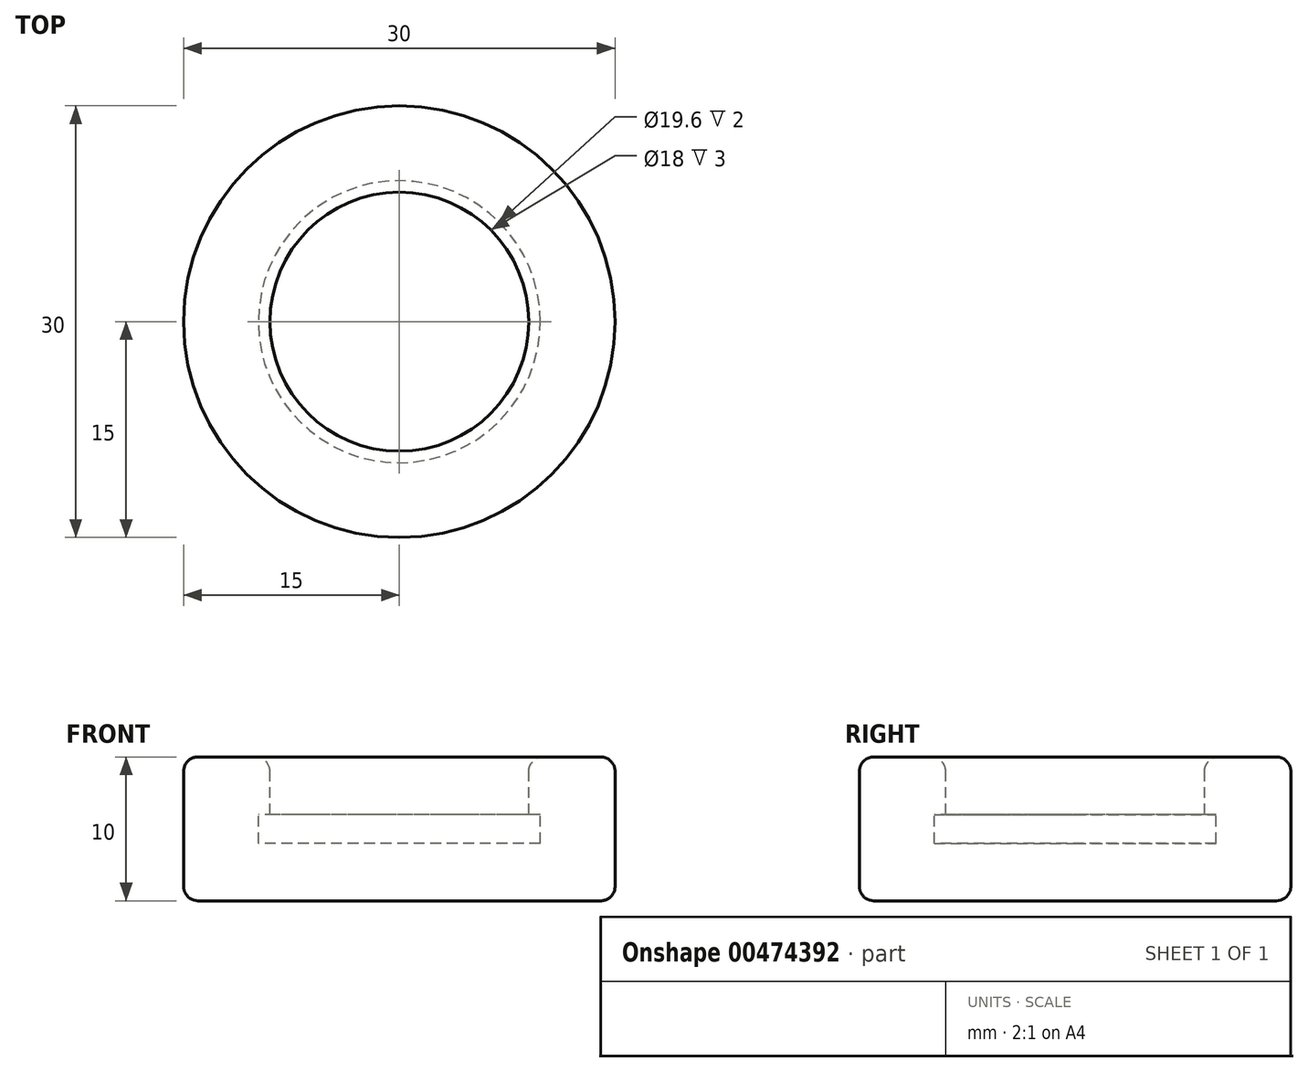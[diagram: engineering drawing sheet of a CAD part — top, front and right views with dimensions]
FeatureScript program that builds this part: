
annotation { "Feature Type Name" : "Feature", "Feature Type Description" : "" }
export const myFeature = defineFeature(function(context is Context, id is Id, definition is map)
    precondition{}
    {
        {
            var Q0;
            Q0=qCreatedBy(makeId("Front.planeOp"),FACE);
            var sketch = newSketch(context, id + "F0", { "sketchPlane" : qUnion([Q0])});
            skLineSegment(sketch, "E0", {"start": v(0, 0) * mm, "end": v(-15, 0) * mm});
            skLineSegment(sketch, "E1", {"start": v(-15, 0) * mm, "end": v(-15, 10) * mm});
            skLineSegment(sketch, "E2", {"start": v(-15, 10) * mm, "end": v(-9, 10) * mm});
            skLineSegment(sketch, "E3", {"start": v(-9, 10) * mm, "end": v(-9, 6) * mm});
            skLineSegment(sketch, "E4", {"start": v(-9, 6) * mm, "end": v(-9.8, 6) * mm});
            skLineSegment(sketch, "E5", {"start": v(-9.8, 6) * mm, "end": v(-9.8, 4) * mm});
            skLineSegment(sketch, "E6", {"start": v(-9.8, 4) * mm, "end": v(0, 4) * mm});
            skLineSegment(sketch, "E7", {"start": v(0, 4) * mm, "end": v(0, 0) * mm});
            skSolve(sketch);
        }
        {
            var Q0;
            Q0=makeQuery(id+"F0.imprint","IMPRINT",FACE,{"disambiguationData":[TD([[makeQuery(id+"F0.imprint","IMPRINT",EDGE,{"derivedFrom":sQuery(id+"F0.wireOp",EDGE,"E0")}),-1.0]])]});
            var Q1;
            Q1=sQuery(id+"F0.wireOp",EDGE,"E7");
            revolve(context, id + "F1", {"entities" : qUnion([Q0]), "axis" : qUnion([Q1]), "revolveType" : RevolveType.FULL});
        }
        {
            var Q0;
            Q0=makeQuery(id+"F1.opRevolve","SWEPT_EDGE",EDGE,{"disambiguationData":[OSD([sQuery(id+"F0.wireOp",EDGE,"E1"),sQuery(id+"F0.wireOp",EDGE,"E2")])]});
            fillet(context, id + "F2", {"entities" : qUnion([Q0]), "radius" : 1 * mm, "tangentPropagation" : true, "allowEdgeOverflow" : false});
        }
        {
            var Q0;
            Q0=makeQuery(id+"F1.opRevolve","SWEPT_EDGE",EDGE,{"disambiguationData":[OSD([sQuery(id+"F0.wireOp",EDGE,"E2"),sQuery(id+"F0.wireOp",EDGE,"E3")])]});
            fillet(context, id + "F3", {"entities" : qUnion([Q0]), "radius" : 1 * mm, "tangentPropagation" : true, "allowEdgeOverflow" : false});
        }
        {
            var Q0;
            Q0=makeQuery(id+"F1.opRevolve","SWEPT_EDGE",EDGE,{"disambiguationData":[OSD([sQuery(id+"F0.wireOp",EDGE,"E0"),sQuery(id+"F0.wireOp",EDGE,"E1")])]});
            fillet(context, id + "F4", {"entities" : qUnion([Q0]), "radius" : 1 * mm, "tangentPropagation" : true, "allowEdgeOverflow" : false});
        }
    });
